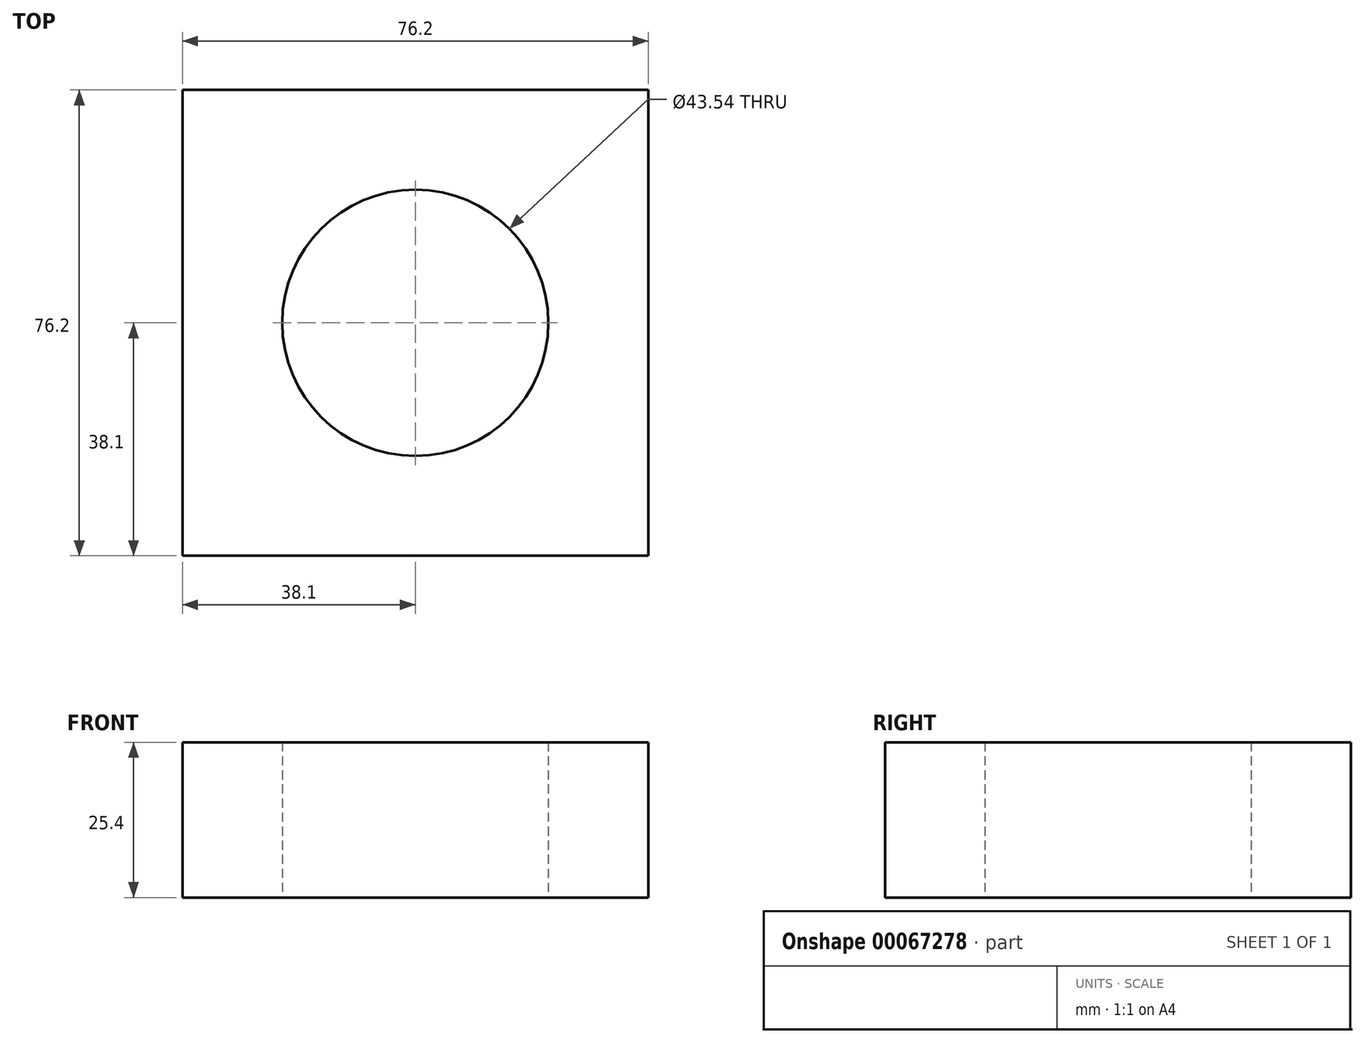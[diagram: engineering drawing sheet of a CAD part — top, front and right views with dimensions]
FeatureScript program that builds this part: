
annotation { "Feature Type Name" : "Feature", "Feature Type Description" : "" }
export const myFeature = defineFeature(function(context is Context, id is Id, definition is map)
    precondition{}
    {
        {
            var Q0;
            Q0=qCreatedBy(makeId("Top.planeOp"),FACE);
            var sketch = newSketch(context, id + "F0", { "sketchPlane" : qUnion([Q0])});
            skLineSegment(sketch, "E0.bottom", {"start": v(0, 0) * mm, "end": v(-76.2, 0) * mm});
            skLineSegment(sketch, "E0.top", {"start": v(0, 76.2) * mm, "end": v(-76.2, 76.2) * mm});
            skLineSegment(sketch, "E0.left", {"start": v(0, 0) * mm, "end": v(0, 76.2) * mm});
            skLineSegment(sketch, "E0.right", {"start": v(-76.2, 0) * mm, "end": v(-76.2, 76.2) * mm});
            skSolve(sketch);
        }
        {
            var Q0;
            Q0=makeQuery(id+"F0.imprint","IMPRINT",FACE,{"disambiguationData":[TD([[makeQuery(id+"F0.imprint","IMPRINT",EDGE,{"derivedFrom":sQuery(id+"F0.wireOp",EDGE,"E0.bottom")}),-1.0]])]});
            extrude(context, id + "F1", {"entities" : qUnion([Q0]), "depth" : 25.4 * mm});
        }
        {
            var Q0;
            Q0=makeQuery(id+"F1.opExtrude","CAP_FACE",FACE,{"disambiguationData":[OSD([sQuery(id+"F0.wireOp",EDGE,"E0.bottom"),sQuery(id+"F0.wireOp",EDGE,"E0.top"),sQuery(id+"F0.wireOp",EDGE,"E0.left"),sQuery(id+"F0.wireOp",EDGE,"E0.right")])],"isStart":true});
            var sketch = newSketch(context, id + "F2", { "sketchPlane" : qUnion([Q0])});
            skCircle(sketch, "E1", {"center": v(-38.1, -38.1) * mm, "radius": 21.77 * mm});
            skLineSegment(sketch, "E2", {"start": v(-76.2, 0) * mm, "end": v(0, -76.2) * mm});
            skLineSegment(sketch, "E3", {"start": v(0, 0) * mm, "end": v(-76.2, -76.2) * mm});
            skSolve(sketch);
        }
        {
            var Q0;
            {var subQ0=sQuery(id+"F2.wireOp",EDGE,"E2");var subQ1=sQuery(id+"F2.wireOp",EDGE,"E1");var subQ2=makeQuery(id+"F2.imprint","INTERSECT",VERTEX,{"disambiguationData":[OD(0.0)],"derivedFrom":[subQ1,subQ0]});Q0=makeQuery(id+"F2.imprint","IMPRINT",FACE,{"disambiguationData":[TD([[makeQuery(id+"F2.imprint","IMPRINT",EDGE,{"disambiguationData":[TD([[subQ2,-1.0]])],"derivedFrom":subQ1}),1.0]])]});}
            var Q1;
            {var subQ0=sQuery(id+"F2.wireOp",EDGE,"E2");var subQ1=sQuery(id+"F2.wireOp",EDGE,"E1");var subQ2=makeQuery(id+"F2.imprint","INTERSECT",VERTEX,{"disambiguationData":[OD(0.0)],"derivedFrom":[subQ1,subQ0]});Q1=makeQuery(id+"F2.imprint","IMPRINT",FACE,{"disambiguationData":[TD([[makeQuery(id+"F2.imprint","IMPRINT",EDGE,{"disambiguationData":[TD([[subQ2,1.0]])],"derivedFrom":subQ1}),1.0]])]});}
            var Q2;
            {var subQ0=sQuery(id+"F2.wireOp",EDGE,"E3");var subQ1=sQuery(id+"F2.wireOp",EDGE,"E1");var subQ2=makeQuery(id+"F2.imprint","INTERSECT",VERTEX,{"disambiguationData":[OD(0.0)],"derivedFrom":[subQ1,subQ0]});Q2=makeQuery(id+"F2.imprint","IMPRINT",FACE,{"disambiguationData":[TD([[makeQuery(id+"F2.imprint","IMPRINT",EDGE,{"disambiguationData":[TD([[subQ2,1.0]])],"derivedFrom":subQ1}),1.0]])]});}
            var Q3;
            {var subQ0=sQuery(id+"F2.wireOp",EDGE,"E3");var subQ1=sQuery(id+"F2.wireOp",EDGE,"E1");var subQ2=makeQuery(id+"F2.imprint","INTERSECT",VERTEX,{"disambiguationData":[OD(1.0)],"derivedFrom":[subQ1,subQ0]});Q3=makeQuery(id+"F2.imprint","IMPRINT",FACE,{"disambiguationData":[TD([[makeQuery(id+"F2.imprint","IMPRINT",EDGE,{"disambiguationData":[TD([[subQ2,-1.0]])],"derivedFrom":subQ1}),1.0]])]});}
            extrude(context, id + "F3", {"entities" : qUnion([Q0, Q1, Q2, Q3]), "operationType" : NewBodyOperationType.REMOVE, "oppositeDirection" : true, "depth" : 54.56 * mm});
        }
    });
